# Revit family: M_Valve_Control_MEPcontent_Oventrop_Cocon QTZ Female-Coupling 1146
name_source: partatom
category: Pipe Accessories
revit_build: Autodesk Revit 2015 (Build: 20140223_1515(x64)
units: mm (PartAtom-declared; Revit-internal decimal feet)

## types (7) — shared parameters
Angle = 75.00°
Article Description = Flow control valve - with pressure test points
Article Type = Cocon QTZ Female-Coupling 1146
Black = Color RGB 35-35-35
Brass = Color RGB 168-128-48
Content Supplier URL = www.mepcontent.eu
Custom = No
Description = Flow control valve - with pressure test points
EMCS Version = 2.0
ETIM Article Class = EC011435
Family Version = 10.14
H3 = 4.421 mm
Hb2 = 7 mm  [stored 0.0229659 ft]
Hb3 = 15 mm
Hb4 = 5 mm  [stored 0.0164042 ft]
Hb5 = 10 mm  [stored 0.0328084 ft]
Hb6 = 6 mm  [stored 0.019685 ft]
Hb7 = 2 mm  [stored 0.00656168 ft]
Hb8 = 2 mm  [stored 0.00656168 ft]
Hb9 = 17 mm
IFCExportAs = IfcValveType
IFCExportType = REGULATING
Lb2 = 5 mm  [stored 0.0164042 ft]
Lb3 = 1.5 mm  [stored 0.00492126 ft]
MEPcontent Class = VALVE_CONTROL
Manufacturer = Oventrop
Manufacturer URL = http://www.oventrop.de
Model = Cocon QTZ Female-Coupling 1146
Pressure Drop = 0.0 Pa
Product Line = Oventrop
Rb3 = 9 mm  [stored 0.0295276 ft]
Rb4 = 16.5 mm
Rb5 = 17.5 mm
Red = Color RGB 255-0-0
Revit Version = 2015
Rv1 = 6 mm  [stored 0.019685 ft]
Rv2 = 9.4 mm  [stored 0.0308399 ft]
Rv3 = 7.7 mm
Rv4 = 5 mm  [stored 0.0164042 ft]
URL = www.stabiplan.com
d1 = 5 mm  [stored 0.0164042 ft]
d2 = 2 mm  [stored 0.00656168 ft]
d3 = 8 mm  [stored 0.0262467 ft]
r1 = 1 mm  [stored 0.00328084 ft]
r2 = 2 mm  [stored 0.00656168 ft]

## per-type parameters (varying)
- DN 20 (150-1050): Arrow_1=4.625 mm; Arrow_2=3.083 mm; GTIN=4026755306699; H4=49.4 mm; H5=4.957 mm; H6=44.7 mm; Hb1=11.2 mm; Height1=52 mm; Height2=48 mm; L1_2=79 mm; L3=15.24 mm; L4=14.288 mm; L5=18.098 mm; LMx=38.25 mm; Lb1=9.25 mm  [stored 0.0303478 ft]; Lb8=13 mm  [stored 0.0426509 ft]; Length1=74 mm; Length2=106 mm; Manufacturer Art. No.=1146006; NominalDiameter1=19.050 mm; NominalDiameter2=19.050 mm; NominalRadius1=9.525 mm; NominalRadius2=9.525 mm; OuterDiameter1=26.9 mm; Ra1=9.525 mm  [stored 0.03125 ft]; Ra1b=8.525 mm  [stored 0.0279692 ft]; Ra2=10.478 mm; Rb1=18.5 mm; Rb1b=19.5 mm; Rb2=21.833 mm; SW1_1=30 mm; SW1_2=30 mm; SW2_1=34.641 mm; SW2_1_05=17.321 mm; SW2_1_051=16.321 mm; SW2_2=34.641 mm; r3=4.523 mm
- DN 15 (30-210): Arrow_1=4.625 mm; Arrow_2=3.083 mm; GTIN=4026755244960; H4=49.4 mm; H5=4.957 mm; H6=44.7 mm; Hb1=11.2 mm; Height1=52 mm; Height2=48 mm; L1_2=75 mm; L3=10.16 mm  [stored 0.0333333 ft]; L4=9.525 mm  [stored 0.03125 ft]; L5=12.065 mm  [stored 0.0395833 ft]; LMx=32.218 mm; Lb1=9.25 mm  [stored 0.0303478 ft]; Lb8=13 mm  [stored 0.0426509 ft]; Length1=70 mm; Length2=98.5 mm; Manufacturer Art. No.=1146004; NominalDiameter1=12.700 mm; NominalDiameter2=12.700 mm; NominalRadius1=6.350 mm; NominalRadius2=6.350 mm; OuterDiameter1=21.3 mm; Ra1=6.35 mm  [stored 0.0208333 ft]; Ra1b=5.35 mm  [stored 0.0175525 ft]; Ra2=6.985 mm; Rb1=18.5 mm; Rb1b=19.5 mm; Rb2=21.833 mm; SW1_1=24 mm; SW1_2=24 mm; SW2_1=27.713 mm; SW2_1_05=13.856 mm; SW2_1_051=12.856 mm; SW2_2=27.713 mm; r3=5.015 mm
- DN 20 (180-1300): Arrow_1=5.203 mm; Arrow_2=3.469 mm; GTIN=4026755347661; H4=55.6 mm; H5=5.577 mm; H6=50.9 mm; Hb1=14.3 mm; Height1=58 mm; Height2=54.5 mm; L1_2=90.5 mm; L3=15.24 mm; L4=14.288 mm; L5=18.098 mm; LMx=40.644 mm; Lb1=10.406 mm; Lb8=14.625 mm; Length1=85.5 mm; Length2=117.5 mm; Manufacturer Art. No.=1146106; NominalDiameter1=19.050 mm; NominalDiameter2=19.050 mm; NominalRadius1=9.525 mm; NominalRadius2=9.525 mm; OuterDiameter1=26.9 mm; Ra1=9.525 mm  [stored 0.03125 ft]; Ra1b=8.525 mm  [stored 0.0279692 ft]; Ra2=10.478 mm; Rb1=20.813 mm; Rb1b=21.813 mm; Rb2=24.146 mm; SW1_1=30 mm; SW1_2=30 mm; SW2_1=34.641 mm; SW2_1_05=17.321 mm; SW2_1_051=16.321 mm; SW2_2=34.641 mm; r3=4.523 mm
- DN 25 (300-2000): Arrow_1=6.706 mm; Arrow_2=4.471 mm; GTIN=4026755340181; H4=63.8 mm; H5=7.188 mm; H6=74.6 mm; Hb1=18.4 mm; Height1=66 mm; Height2=79 mm; L1_2=123 mm; L3=20.32 mm; L4=19.05 mm; L5=24.13 mm; LMx=52.901 mm; Lb1=13.413 mm; Lb8=18.85 mm; Length1=118 mm; Length2=154 mm; Manufacturer Art. No.=1146108; NominalDiameter1=25.400 mm; NominalDiameter2=25.400 mm; NominalRadius1=12.700 mm; NominalRadius2=12.700 mm; OuterDiameter1=33.7 mm; Ra1=12.7 mm  [stored 0.0416667 ft]; Ra1b=11.7 mm; Ra2=13.97 mm; Rb1=26.825 mm; Rb1b=27.825 mm; Rb2=30.158 mm; SW1_1=36 mm; SW1_2=36 mm; SW2_1=41.569 mm; SW2_1_05=20.785 mm; SW2_1_051=19.785 mm; SW2_2=41.569 mm; r3=4.03 mm
- DN 32 (600-3600): Arrow_1=6.706 mm; Arrow_2=4.471 mm; GTIN=4026755340198; H4=63.8 mm; H5=7.188 mm; H6=74.6 mm; Hb1=18.4 mm; Height1=66 mm; Height2=79 mm; L1_2=129 mm; L3=25.4 mm; L4=23.813 mm; L5=30.163 mm; LMx=58.934 mm; Lb1=13.413 mm; Lb8=18.85 mm; Length1=124 mm; Length2=165 mm; Manufacturer Art. No.=1146110; NominalDiameter1=31.750 mm; NominalDiameter2=31.750 mm; NominalRadius1=15.875 mm; NominalRadius2=15.875 mm; OuterDiameter1=42.4 mm; Ra1=15.875 mm; Ra1b=14.875 mm; Ra2=17.463 mm; Rb1=26.825 mm; Rb1b=27.825 mm; Rb2=30.158 mm; SW1_1=45 mm; SW1_2=45 mm; SW2_1=51.962 mm; SW2_1_05=25.981 mm; SW2_1_051=24.981 mm; SW2_2=51.962 mm; r3=5.038 mm
- DN 15 (90-450): Arrow_1=4.625 mm; Arrow_2=3.083 mm; GTIN=4026755244977; H4=49.4 mm; H5=4.957 mm; H6=44.7 mm; Hb1=11.2 mm; Height1=52 mm; Height2=48 mm; L1_2=75 mm; L3=10.16 mm  [stored 0.0333333 ft]; L4=9.525 mm  [stored 0.03125 ft]; L5=12.065 mm  [stored 0.0395833 ft]; LMx=32.218 mm; Lb1=9.25 mm  [stored 0.0303478 ft]; Lb8=13 mm  [stored 0.0426509 ft]; Length1=70 mm; Length2=98.5 mm; Manufacturer Art. No.=1146104; NominalDiameter1=12.700 mm; NominalDiameter2=12.700 mm; NominalRadius1=6.350 mm; NominalRadius2=6.350 mm; OuterDiameter1=21.3 mm; Ra1=6.35 mm  [stored 0.0208333 ft]; Ra1b=5.35 mm  [stored 0.0175525 ft]; Ra2=6.985 mm; Rb1=18.5 mm; Rb1b=19.5 mm; Rb2=21.833 mm; SW1_1=24 mm; SW1_2=24 mm; SW2_1=27.713 mm; SW2_1_05=13.856 mm; SW2_1_051=12.856 mm; SW2_2=27.713 mm; r3=5.015 mm
- DN 15 (150-1050): Arrow_1=4.625 mm; Arrow_2=3.083 mm; GTIN=4026755244984; H4=49.4 mm; H5=4.957 mm; H6=44.7 mm; Hb1=11.2 mm; Height1=52 mm; Height2=48 mm; L1_2=75 mm; L3=10.16 mm  [stored 0.0333333 ft]; L4=9.525 mm  [stored 0.03125 ft]; L5=12.065 mm  [stored 0.0395833 ft]; LMx=32.218 mm; Lb1=9.25 mm  [stored 0.0303478 ft]; Lb8=13 mm  [stored 0.0426509 ft]; Length1=70 mm; Length2=98.5 mm; Manufacturer Art. No.=1146204; NominalDiameter1=12.700 mm; NominalDiameter2=12.700 mm; NominalRadius1=6.350 mm; NominalRadius2=6.350 mm; OuterDiameter1=21.3 mm; Ra1=6.35 mm  [stored 0.0208333 ft]; Ra1b=5.35 mm  [stored 0.0175525 ft]; Ra2=6.985 mm; Rb1=18.5 mm; Rb1b=19.5 mm; Rb2=21.833 mm; SW1_1=24 mm; SW1_2=24 mm; SW2_1=27.713 mm; SW2_1_05=13.856 mm; SW2_1_051=12.856 mm; SW2_2=27.713 mm; r3=5.015 mm

note: [stored X ft] marks values corroborated as IEEE doubles in the binary element streams (Revit-internal decimal feet)

## geometry (parser evidence)
native form markers: Blend x4, Sweep x1
no freeform markers — native parametric forms only
